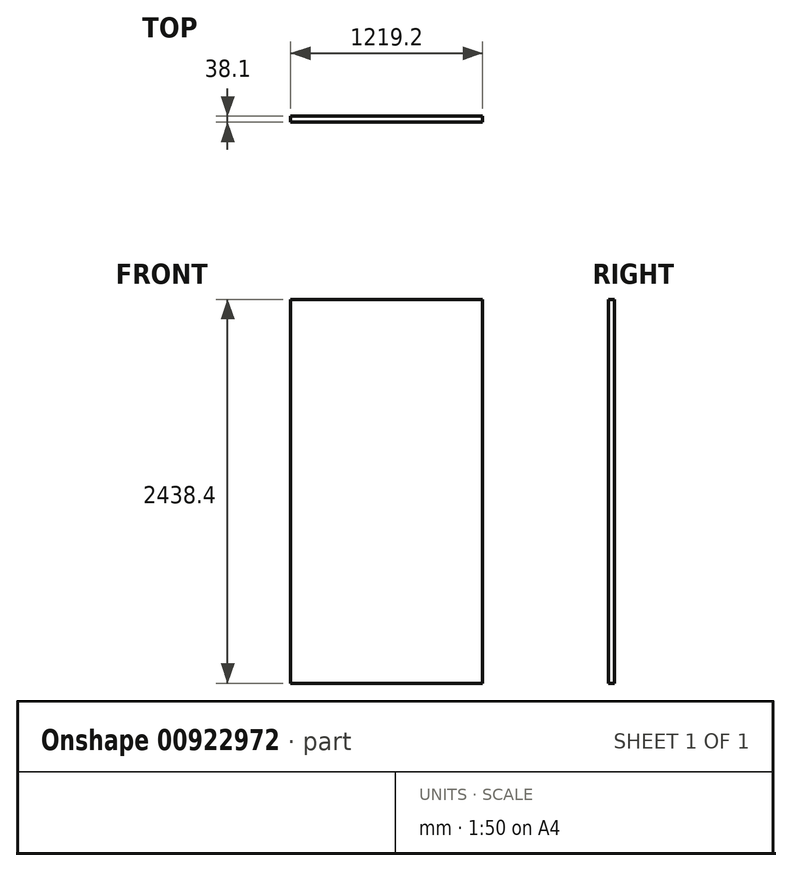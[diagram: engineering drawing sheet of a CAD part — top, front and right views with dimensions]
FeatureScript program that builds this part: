
annotation { "Feature Type Name" : "Feature", "Feature Type Description" : "" }
export const myFeature = defineFeature(function(context is Context, id is Id, definition is map)
    precondition{}
    {
        {
            var Q0;
            Q0=qCreatedBy(makeId("Front.planeOp"),FACE);
            var sketch = newSketch(context, id + "F0", { "sketchPlane" : qUnion([Q0])});
            skLineSegment(sketch, "E0.rect.bottom", {"start": v(-609.6, 1219.2) * mm, "end": v(609.6, 1219.2) * mm});
            skLineSegment(sketch, "E0.rect.top", {"start": v(-609.6, -1219.2) * mm, "end": v(609.6, -1219.2) * mm});
            skLineSegment(sketch, "E0.rect.left", {"start": v(-609.6, 1219.2) * mm, "end": v(-609.6, -1219.2) * mm});
            skLineSegment(sketch, "E0.rect.right", {"start": v(609.6, 1219.2) * mm, "end": v(609.6, -1219.2) * mm});
            skPoint(sketch, "E0.rect.middle", {"position": v(0, 0) * mm});
            skPoint(sketch, "E1.rect.middle", {"position": v(171.45, 52.39) * mm});
            skSolve(sketch);
        }
        {
            var Q0;
            Q0 = qSketchRegion(id + "F0", true);
            extrude(context, id + "F1", {"entities" : qUnion([Q0]), "depth" : 38.1 * mm, "offsetDistance" : 25.4 * mm});
        }
    });
